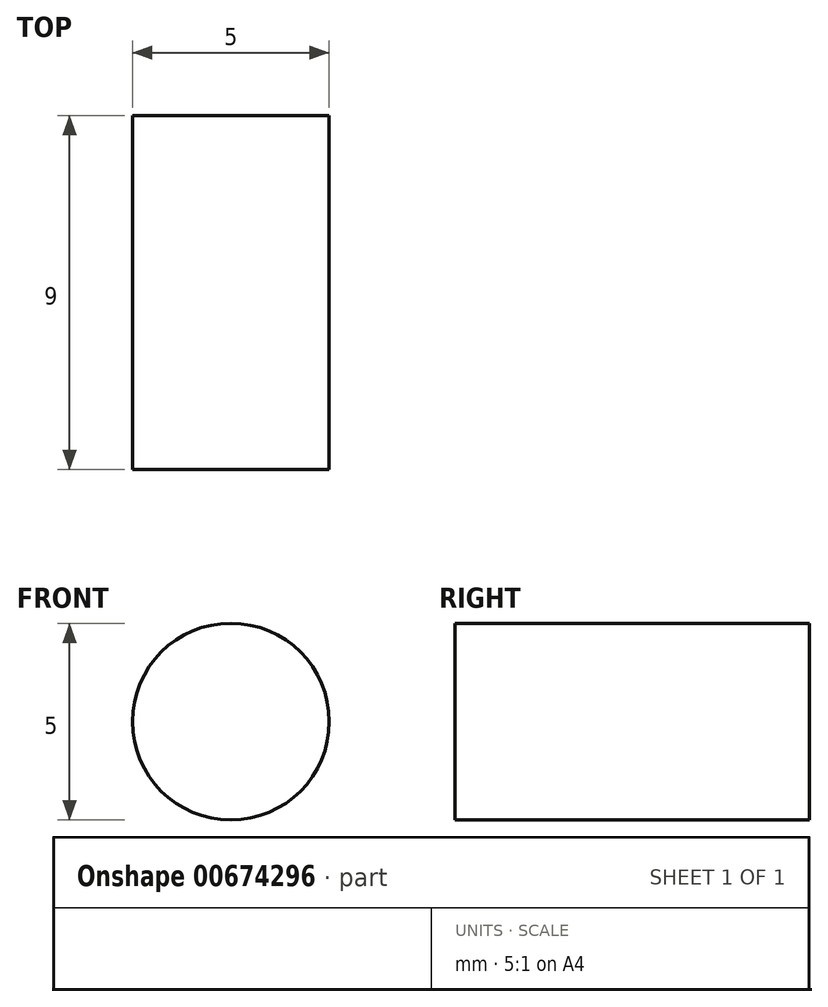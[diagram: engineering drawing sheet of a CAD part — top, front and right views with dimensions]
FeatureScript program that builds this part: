
annotation { "Feature Type Name" : "Feature", "Feature Type Description" : "" }
export const myFeature = defineFeature(function(context is Context, id is Id, definition is map)
    precondition{}
    {
        {
            var Q0;
            Q0=qCreatedBy(makeId("Front.planeOp"),FACE);
            var sketch = newSketch(context, id + "F0", { "sketchPlane" : qUnion([Q0])});
            skCircle(sketch, "E0", {"center": v(0, 0) * mm, "radius": 2.5 * mm});
            skSolve(sketch);
        }
        {
            var Q0;
            Q0 = qSketchRegion(id + "F0", true);
            extrude(context, id + "F1", {"entities" : qUnion([Q0]), "depth" : 9 * mm, "offsetDistance" : 25 * mm});
        }
    });
